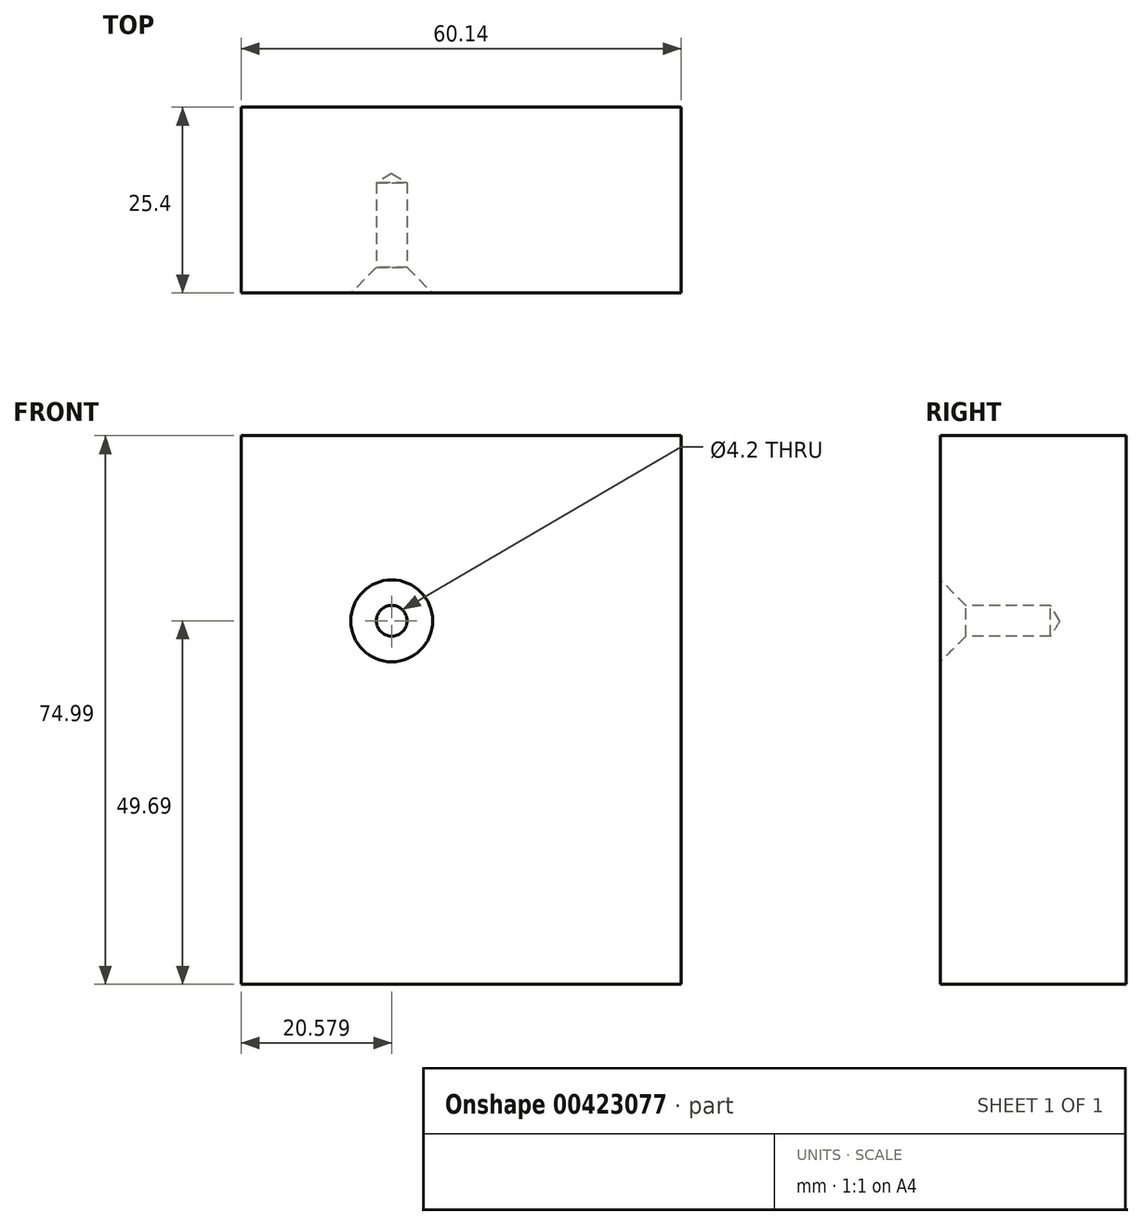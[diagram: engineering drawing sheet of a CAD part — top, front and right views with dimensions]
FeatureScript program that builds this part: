
annotation { "Feature Type Name" : "Feature", "Feature Type Description" : "" }
export const myFeature = defineFeature(function(context is Context, id is Id, definition is map)
    precondition{}
    {
        {
            var Q0;
            Q0=qCreatedBy(makeId("Front.planeOp"),FACE);
            var sketch = newSketch(context, id + "F0", { "sketchPlane" : qUnion([Q0])});
            skLineSegment(sketch, "E0.bottom", {"start": v(60.44, 57.06) * mm, "end": v(-93, 57.06) * mm});
            skLineSegment(sketch, "E0.top", {"start": v(60.44, -68.77) * mm, "end": v(-93, -68.77) * mm});
            skLineSegment(sketch, "E0.left", {"start": v(60.44, 57.06) * mm, "end": v(60.44, -68.77) * mm});
            skLineSegment(sketch, "E0.right", {"start": v(-93, 57.06) * mm, "end": v(-93, -68.77) * mm});
            skLineSegment(sketch, "E1.bottom", {"start": v(-93, 57.06) * mm, "end": v(-32.86, 57.06) * mm});
            skLineSegment(sketch, "E1.top", {"start": v(-93, -17.93) * mm, "end": v(-32.86, -17.93) * mm});
            skLineSegment(sketch, "E1.left", {"start": v(-93, 57.06) * mm, "end": v(-93, -17.93) * mm});
            skLineSegment(sketch, "E1.right", {"start": v(-32.86, 57.06) * mm, "end": v(-32.86, -17.93) * mm});
            skLineSegment(sketch, "E2.0", {"start": v(-93, 50.7) * mm, "end": v(-32.86, 50.7) * mm});
            skSolve(sketch);
        }
        {
            var Q0;
            {var subQ0=sQuery(id+"F0.wireOp",EDGE,"E1.top");Q0=makeQuery(id+"F0.imprint","IMPRINT",FACE,{"disambiguationData":[TD([[makeQuery(id+"F0.imprint","IMPRINT",EDGE,{"derivedFrom":subQ0}),1.0]])]});}
            var Q1;
            {var subQ0=sQuery(id+"F0.wireOp",EDGE,"E0.bottom");Q1=makeQuery(id+"F0.imprint","IMPRINT",FACE,{"disambiguationData":[TD([[makeQuery(id+"F0.imprint","IMPRINT",EDGE,{"derivedFrom":subQ0}),1.0]])]});}
            var Q2;
            {var subQ0=sQuery(id+"F0.wireOp",EDGE,"E1.bottom");Q2=makeQuery(id+"F0.imprint","IMPRINT",FACE,{"disambiguationData":[TD([[makeQuery(id+"F0.imprint","IMPRINT",EDGE,{"derivedFrom":subQ0}),-1.0]])]});}
            extrude(context, id + "F1", {"entities" : qUnion([Q0, Q1, Q2]), "depth" : 25.4 * mm});
        }
        {
            var Q0;
            Q0=makeQuery(id+"F1.opExtrude","CAP_FACE",FACE,{"disambiguationData":[OSD([sQuery(id+"F0.wireOp",EDGE,"E0.bottom"),sQuery(id+"F0.wireOp",EDGE,"E0.top"),sQuery(id+"F0.wireOp",EDGE,"E0.left"),sQuery(id+"F0.wireOp",EDGE,"E0.right"),sQuery(id+"F0.wireOp",EDGE,"E1.bottom"),sQuery(id+"F0.wireOp",EDGE,"E1.left")])],"isStart":false});
            var sketch = newSketch(context, id + "F2", { "sketchPlane" : qUnion([Q0])});
            skPoint(sketch, "E3", {"position": v(-72.42, 31.76) * mm});
            skPoint(sketch, "E4", {"position": v(-24.97, 0) * mm});
            skPoint(sketch, "E5", {"position": v(-76.63, -59.55) * mm});
            skSolve(sketch);
        }
        {
            var Q0;
            Q0=sQuery(id+"F2.wireOp",VERTEX,"E3");
            var Q1;
            Q1=makeQuery(id+"F1.opExtrude","SWEPT_BODY",BODY,{"disambiguationData":[OSD([sQuery(id+"F0.wireOp",EDGE,"E0.bottom"),sQuery(id+"F0.wireOp",EDGE,"E0.top"),sQuery(id+"F0.wireOp",EDGE,"E0.left"),sQuery(id+"F0.wireOp",EDGE,"E0.right"),sQuery(id+"F0.wireOp",EDGE,"E1.bottom"),sQuery(id+"F0.wireOp",EDGE,"E1.left")])]});
            hole(context, id + "F3", {"style" : HoleStyle.C_SINK, "endStyle" : HoleEndStyle.BLIND, "holeDiameter" : 4.2 * mm, "cSinkDiameter" : 11.2 * mm, "cSinkAngle" : 90 * degree, "holeDepth" : 15.1 * mm, "isTappedThrough" : true, "tappedDepth" : 12.7 * mm, "tapClearance" : 3, "locations" : qUnion([Q0]), "scope" : qUnion([Q1])});
        }
    });
